# Revit family: Wall_Cabinets-Teknion-RHWHDG_Wall_Cabinet_with_Pigeonhole_Section_and_Glass_Doors-R2018
name_source: partatom
category: Furniture
revit_build: Autodesk Revit 2018 (Build: 20190510_1515(x64)
units: mm (PartAtom-declared; Revit-internal decimal feet)

## family parameters
Always vertical = Yes
Cut with Voids When Loaded = No
OmniClass Number = 23.40.20.00
OmniClass Title = General Furniture and Specialties
Room Calculation Point = No
Shared = Yes
Work Plane-Based = No

## types (3) — shared parameters
Assembly Code = E2020200
Case Finish = Source Laminate - Teknion - 3M - Provincial Oak
Door Finish = Paint - Teknion - Mica - Platinum
For Additional Finishes please visit = https://assets.teknion.com
Glass Finish = Glass - Teknion - FT - Frosted Glass
Manufacturer = Teknion
Manufacturer Fax = 416.661.4586
Part Number = RHWHDG
Product Documentation Link = https://www.teknion.com
Product Line = Modular Cabinets
Product Page URL = https://www.teknion.com
Series = Modular Cabinets
Sustainability Data = https://www.teknion.com
To render please download texture images found here = https://assets.teknion.com
URL = www.teknion.com
Unit Weight URL = http://www.teknion.com
Warranty = http://www.teknion.com

## per-type parameters (varying)
| type | Description | Horizontal Shelf | Horizontal Shelf Spacing 1 | Horizontal Shelf Spacing 2 | Horizontal Shelf Thickness | Laminate Horizontal | Laminate Vertical | Material Note | Model | Shelf Finish |
| Laminate Horizontal Divider | Wall Cabinet with Pigeonhole Section and Glass Doors, Laminate Horizontal Divider, 15" Depth | Yes | 10.829 " | 6.265 " | 0.701 " | Yes | No | Shelf Finish must match Case Finish | RHWHDGH15_____ | Source Laminate - Teknion - 3M - Provincial Oak |
| Laminate Vertical Divider | Wall Cabinet with Pigeonhole Section and Glass Doors, Laminate Vertical Divider, 15" Depth | No | 10.572 " | 6.136 " | 0.315 " | No | Yes | Shelf Finish must match Case Finish | RHWHDGV15_____ | Source Laminate - Teknion - 3M - Provincial Oak |
| Metal Horizontal Divider | Wall Cabinet with Pigeonhole Section and Glass Doors, Metal Horizontal Divider,15" Depth | Yes | 10.572 " | 6.136 " | 0.315 " | No | No | Shelf Finish must be Metal Finish coordinated with Case Finish | RHWHDGM15_____ | Paint - Teknion - Mica - Sepia Bronze |

## geometry (parser evidence)
native form markers: Sweep x2
no freeform markers — native parametric forms only
